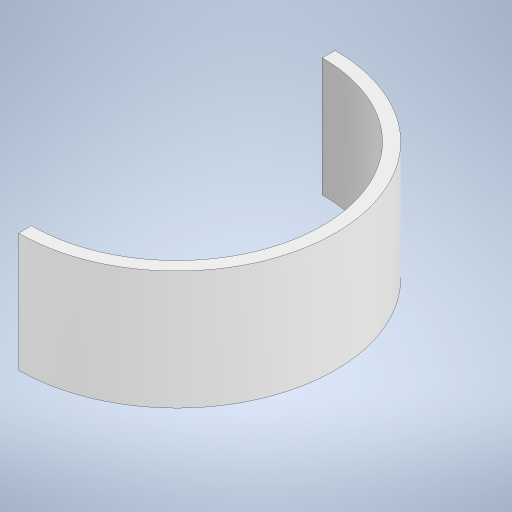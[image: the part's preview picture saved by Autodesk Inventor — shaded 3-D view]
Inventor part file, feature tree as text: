
AUTODESK INVENTOR PART (.ipt)
format: ipt  version: 2023 (Build 270158000, 158)  size: 568,320 bytes
history: native  units: mm
features: extrude x2, sketch x1
ambient origin geometry x8: Origin, YZ Plane, XZ Plane, XY Plane, X Axis, Y Axis, Z Axis, Center Point
bodies: Solid1 (feature_tree)
feature tree (3):
  extrude  "Extrusion1"  Depth=60.0mm
  extrude  "Extrusion4"  Depth=60.0mm TaperAngle=0.0deg
  sketch  "Sketch3"  dims[d0=160.0mm d1=3.0mm d2=60.0mm d3=0.0mm d11=147.0mm d12=60.0mm d13=0.0mm]
